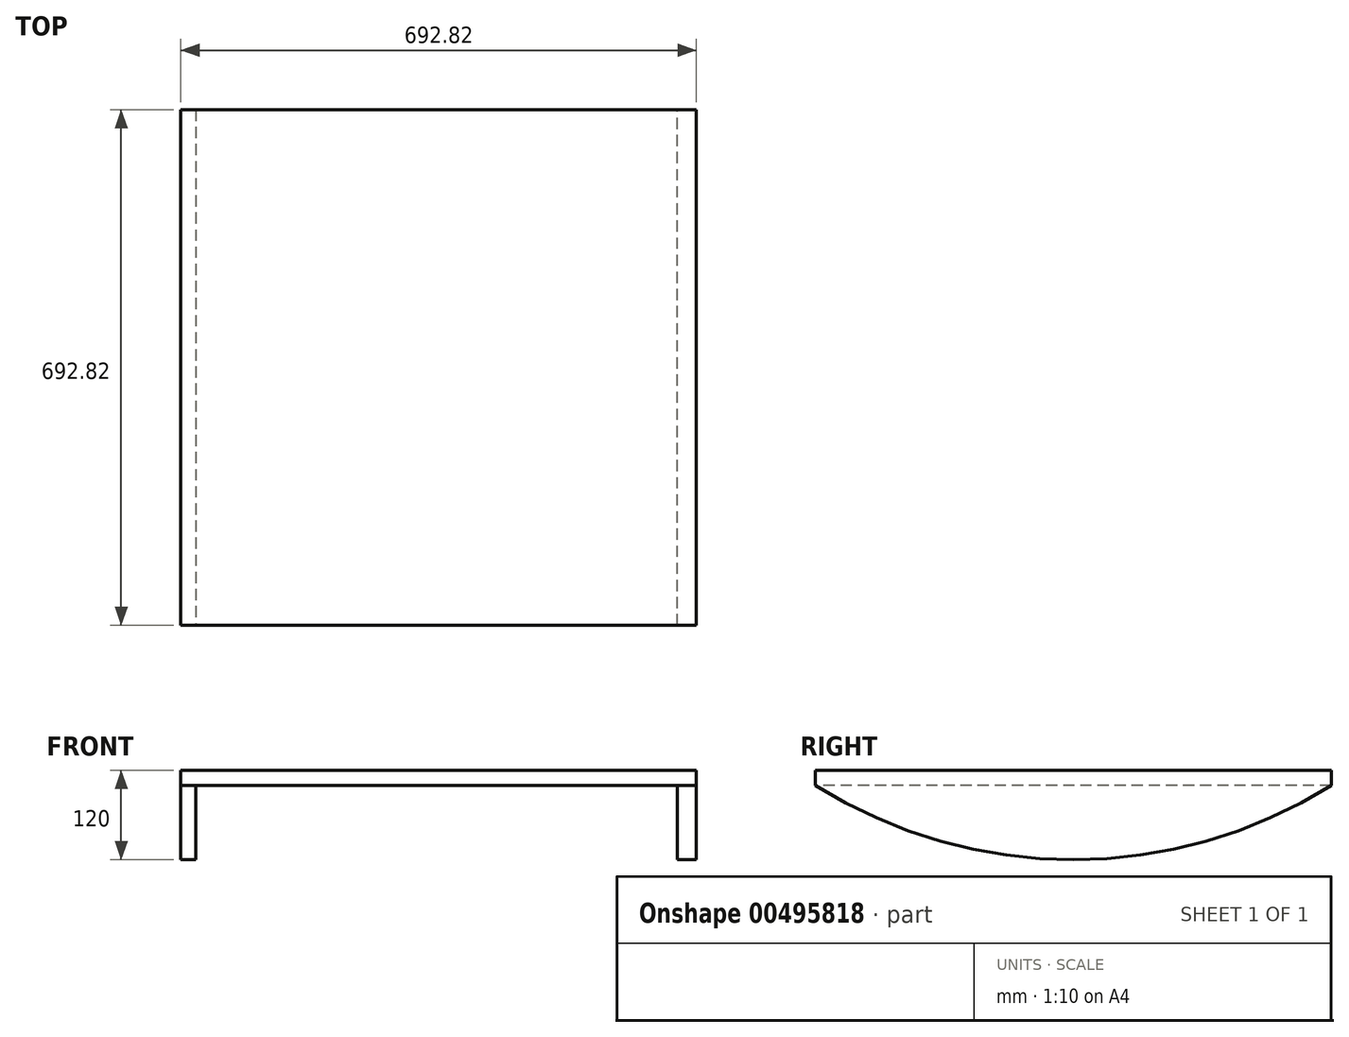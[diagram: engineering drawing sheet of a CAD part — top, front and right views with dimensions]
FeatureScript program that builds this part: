
annotation { "Feature Type Name" : "Feature", "Feature Type Description" : "" }
export const myFeature = defineFeature(function(context is Context, id is Id, definition is map)
    precondition{}
    {
        {
            var Q0;
            Q0=qCreatedBy(makeId("Right.planeOp"),FACE);
            var sketch = newSketch(context, id + "F0", { "sketchPlane" : qUnion([Q0])});
            skArc(sketch, "E0", {"start": v(-346.41, -550) * mm, "mid": v(0, -650) * mm, "end": v(346.41, -550) * mm});
            skLineSegment(sketch, "E1", {"start": v(-346.41, -550) * mm, "end": v(346.41, -550) * mm});
            skPoint(sketch, "E2.orphan", {"position": v(-650, 0) * mm});
            skSolve(sketch);
        }
        {
            var Q0;
            Q0 = qSketchRegion(id + "F0", true);
            extrude(context, id + "F1", {"entities" : qUnion([Q0]), "depth" : 25.4 * mm});
        }
        {
            var Q0;
            Q0=makeQuery(id+"F1.opExtrude","SWEPT_FACE",FACE,{"disambiguationData":[OSD([sQuery(id+"F0.wireOp",EDGE,"E1")])]});
            var sketch = newSketch(context, id + "F2", { "sketchPlane" : qUnion([Q0])});
            skLineSegment(sketch, "E3.bottom", {"start": v(25.4, 346.41) * mm, "end": v(-667.42, 346.41) * mm});
            skLineSegment(sketch, "E3.top", {"start": v(25.4, -346.41) * mm, "end": v(-667.42, -346.41) * mm});
            skLineSegment(sketch, "E3.left", {"start": v(25.4, 346.41) * mm, "end": v(25.4, -346.41) * mm});
            skLineSegment(sketch, "E3.right", {"start": v(-667.42, 346.41) * mm, "end": v(-667.42, -346.41) * mm});
            skSolve(sketch);
        }
        {
            var Q0;
            Q0 = qSketchRegion(id + "F2", true);
            var Q1;
            {var subQ2=sQuery(id+"F2.wireOp",EDGE,"E3.right");Q1=makeQuery(id+"F2.imprint","IMPRINT",FACE,{"disambiguationData":[TD([[makeQuery(id+"F2.imprint","IMPRINT",EDGE,{"derivedFrom":subQ2}),1.0]])]});}
            extrude(context, id + "F3", {"entities" : qUnion([Q0, Q1]), "operationType" : NewBodyOperationType.ADD, "depth" : 20 * mm});
        }
        {
            var Q0;
            Q0=makeQuery(id+"F3.opExtrude","SWEPT_FACE",FACE,{"disambiguationData":[OSD([sQuery(id+"F2.wireOp",EDGE,"E3.right")])]});
            var sketch = newSketch(context, id + "F4", { "sketchPlane" : qUnion([Q0])});
            skArc(sketch, "E4", {"start": v(-346.41, -550) * mm, "mid": v(0, -650) * mm, "end": v(346.41, -550) * mm});
            skLineSegment(sketch, "E5", {"start": v(-346.41, -550) * mm, "end": v(346.41, -550) * mm});
            skSolve(sketch);
        }
        {
            var Q0;
            Q0=makeQuery(id+"F4.imprint","IMPRINT",FACE,{"disambiguationData":[TD([[makeQuery(id+"F4.imprint","IMPRINT",EDGE,{"derivedFrom":sQuery(id+"F4.wireOp",EDGE,"E4")}),1.0]])]});
            extrude(context, id + "F5", {"entities" : qUnion([Q0]), "oppositeDirection" : true, "depth" : 20 * mm});
        }
    });
